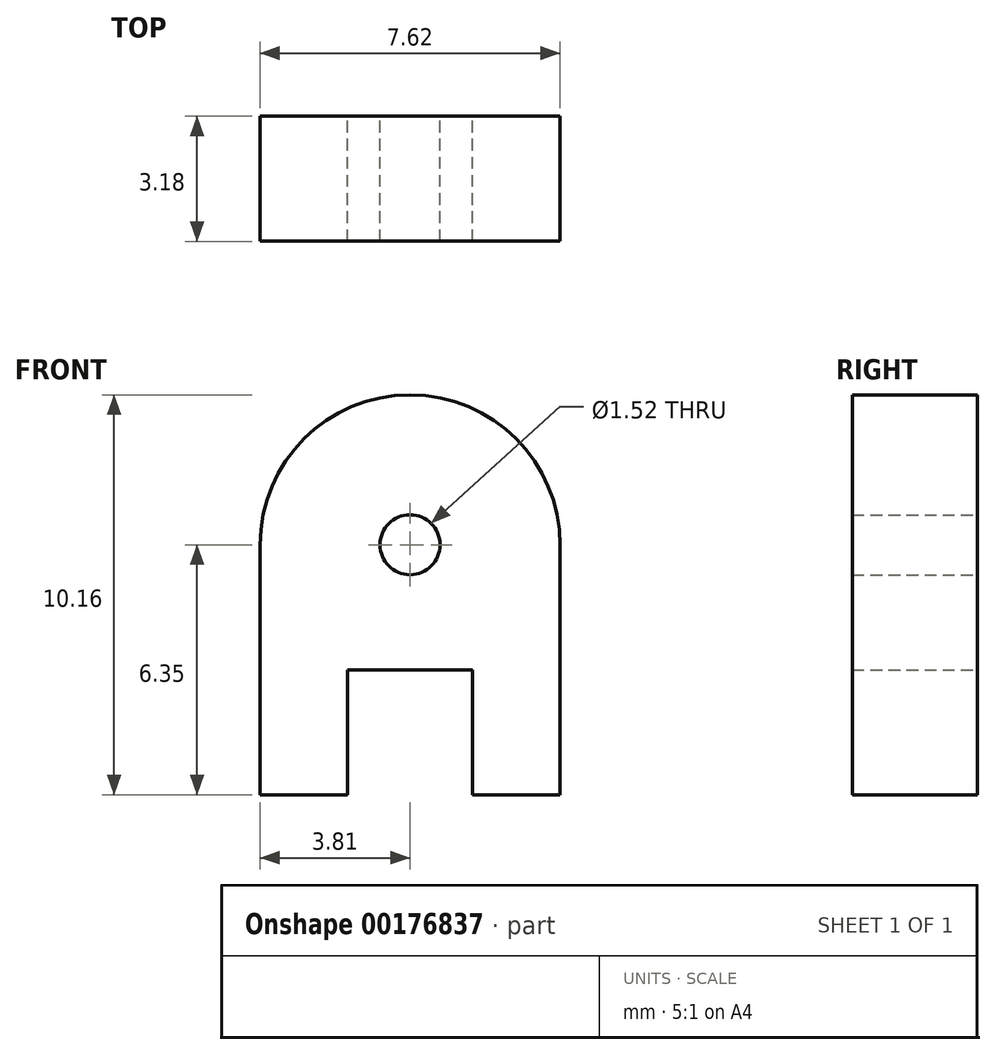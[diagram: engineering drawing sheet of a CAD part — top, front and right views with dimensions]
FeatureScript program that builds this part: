
annotation { "Feature Type Name" : "Feature", "Feature Type Description" : "" }
export const myFeature = defineFeature(function(context is Context, id is Id, definition is map)
    precondition{}
    {
        {
            var Q0;
            Q0=qCreatedBy(makeId("Front.planeOp"),FACE);
            var sketch = newSketch(context, id + "F0", { "sketchPlane" : qUnion([Q0])});
            skLineSegment(sketch, "E0", {"start": v(-3.81, 0) * mm, "end": v(-3.81, 6.35) * mm});
            skArc(sketch, "E1", {"start": v(3.81, 6.35) * mm, "mid": v(0, 10.16) * mm, "end": v(-3.81, 6.35) * mm});
            skLineSegment(sketch, "E2", {"start": v(3.8, 6.35) * mm, "end": v(3.81, 0) * mm});
            skLineSegment(sketch, "E3", {"start": v(3.81, 0) * mm, "end": v(1.59, 0) * mm});
            skLineSegment(sketch, "E4", {"start": v(1.59, 0) * mm, "end": v(1.59, 3.17) * mm});
            skLineSegment(sketch, "E5", {"start": v(1.59, 3.17) * mm, "end": v(-1.59, 3.17) * mm});
            skLineSegment(sketch, "E6", {"start": v(-1.59, 3.17) * mm, "end": v(-1.59, 0) * mm});
            skLineSegment(sketch, "E7", {"start": v(-1.59, 0) * mm, "end": v(-3.81, 0) * mm});
            skLineSegment(sketch, "E8", {"start": v(0, 0) * mm, "end": v(0, 6.35) * mm, "construction": true});
            skSolve(sketch);
        }
        {
            var Q0;
            Q0 = qSketchRegion(id + "F0", true);
            extrude(context, id + "F1", {"entities" : qUnion([Q0]), "depth" : 3.17 * mm});
        }
        {
            var Q0;
            Q0=sQuery(id+"F0.wireOp",VERTEX,"E1.center");
            var Q1;
            Q1=makeQuery(id+"F1.opExtrude","SWEPT_BODY",BODY,{"disambiguationData":[OSD([sQuery(id+"F0.wireOp",EDGE,"E0"),sQuery(id+"F0.wireOp",EDGE,"E1"),sQuery(id+"F0.wireOp",EDGE,"E2"),sQuery(id+"F0.wireOp",EDGE,"E3"),sQuery(id+"F0.wireOp",EDGE,"E4"),sQuery(id+"F0.wireOp",EDGE,"E5"),sQuery(id+"F0.wireOp",EDGE,"E6"),sQuery(id+"F0.wireOp",EDGE,"E7")])]});
            hole(context, id + "F2", {"style" : HoleStyle.SIMPLE, "endStyle" : HoleEndStyle.THROUGH, "oppositeDirection" : true, "holeDiameter" : 1.52 * mm, "locations" : qUnion([Q0]), "scope" : qUnion([Q1]), "isTappedThrough" : true});
        }
    });
